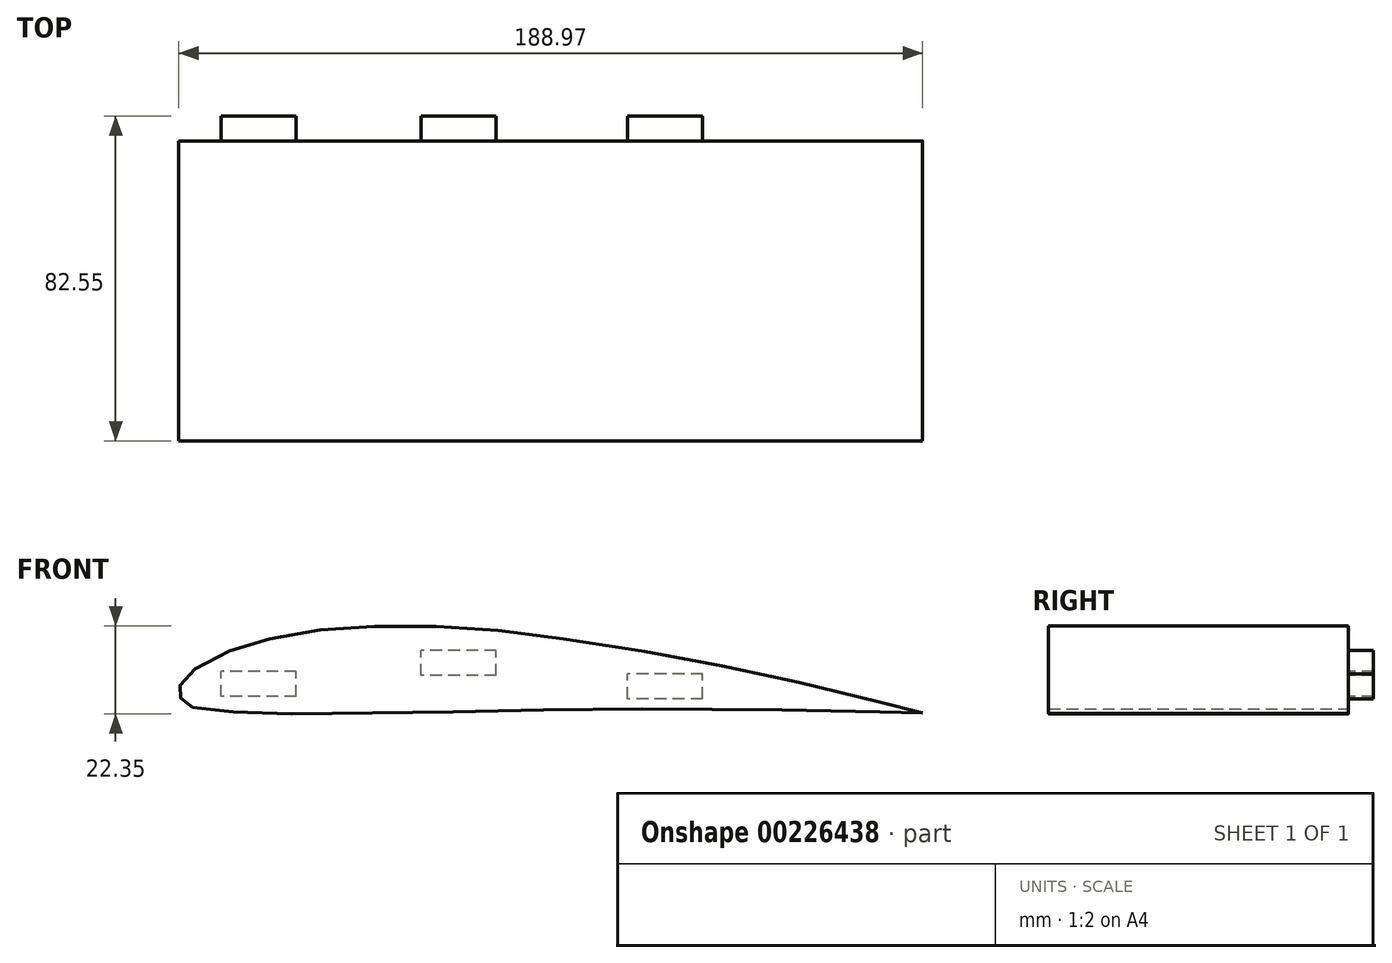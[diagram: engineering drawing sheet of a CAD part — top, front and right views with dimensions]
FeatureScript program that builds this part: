
annotation { "Feature Type Name" : "Feature", "Feature Type Description" : "" }
export const myFeature = defineFeature(function(context is Context, id is Id, definition is map)
    precondition{}
    {
        {
            var Q0;
            Q0=qCreatedBy(makeId("Front.planeOp"),FACE);
            var sketch = newSketch(context, id + "F0", { "sketchPlane" : qUnion([Q0])});
            skFitSpline(sketch, "E0.0", {"points": [v(113.13, -7.74) * mm, v(113.1, -7.8) * mm, v(110.34, -7.7) * mm, v(99.32, -7.43) * mm, v(55.98, -6.77) * mm, v(16.87, -7.02) * mm, v(15.68, -7.03) * mm, v(-47.47, -7.98) * mm, v(-59.24, -7.55) * mm, v(-66.72, -7.33) * mm, v(-71.5, -6.53) * mm, v(-72.72, -6.16) * mm, v(-73.48, -5.82) * mm, v(-74.18, -5.33) * mm, v(-74.78, -4.74) * mm, v(-75.21, -4.15) * mm, v(-75.5, -3.61) * mm, v(-75.69, -3.09) * mm, v(-75.76, -2.76) * mm, v(-75.8, -2.28) * mm, v(-75.77, -1.79) * mm, v(-75.64, -1.22) * mm, v(-75.39, -0.56) * mm, v(-74.8, 0.42) * mm, v(-73.97, 1.42) * mm, v(-72.44, 2.82) * mm, v(-70, 4.46) * mm, v(-65.33, 6.96) * mm, v(-60.69, 8.94) * mm, v(-55.6, 10.4) * mm, v(-48, 12.06) * mm, v(-39.71, 13.3) * mm, v(-30.48, 14.09) * mm, v(-19.95, 14.34) * mm, v(-7.36, 14.13) * mm, v(4.86, 13.21) * mm, v(17.45, 11.72) * mm, v(37.4, 8.66) * mm, v(57.72, 5.15) * mm, v(75.8, 1.3) * mm, v(97.79, -3.81) * mm, v(110.28, -7.09) * mm, v(113.15, -7.68) * mm, v(113.13, -7.74) * mm]});
            skPoint(sketch, "E1", {"position": v(-75.8, -2.17) * mm});
            skPoint(sketch, "E2", {"position": v(112.92, -7.77) * mm});
            skLineSegment(sketch, "E3.bottom", {"start": v(-45.95, -3.58) * mm, "end": v(-65, -3.58) * mm});
            skLineSegment(sketch, "E3.top", {"start": v(-45.95, 2.77) * mm, "end": v(-65, 2.77) * mm});
            skLineSegment(sketch, "E3.left", {"start": v(-45.95, -3.58) * mm, "end": v(-45.95, 2.77) * mm});
            skLineSegment(sketch, "E3.right", {"start": v(-65, -3.58) * mm, "end": v(-65, 2.77) * mm});
            skPoint(sketch, "E3.middle", {"position": v(-55.47, -0.4) * mm});
            skLineSegment(sketch, "E4.bottom", {"start": v(4.85, 1.75) * mm, "end": v(-14.2, 1.75) * mm});
            skLineSegment(sketch, "E4.top", {"start": v(4.85, 8.1) * mm, "end": v(-14.2, 8.1) * mm});
            skLineSegment(sketch, "E4.left", {"start": v(4.85, 1.75) * mm, "end": v(4.85, 8.1) * mm});
            skLineSegment(sketch, "E4.right", {"start": v(-14.2, 1.75) * mm, "end": v(-14.2, 8.1) * mm});
            skPoint(sketch, "E4.middle", {"position": v(-4.67, 4.93) * mm});
            skLineSegment(sketch, "E5.bottom", {"start": v(57.28, -4.16) * mm, "end": v(38.23, -4.16) * mm});
            skLineSegment(sketch, "E5.top", {"start": v(57.28, 2.2) * mm, "end": v(38.23, 2.2) * mm});
            skLineSegment(sketch, "E5.left", {"start": v(57.28, -4.16) * mm, "end": v(57.28, 2.2) * mm});
            skLineSegment(sketch, "E5.right", {"start": v(38.23, -4.16) * mm, "end": v(38.23, 2.2) * mm});
            skPoint(sketch, "E5.middle", {"position": v(47.76, -0.98) * mm});
            skLineSegment(sketch, "E6", {"start": v(112.92, -7.77) * mm, "end": v(-97.83, -7.77) * mm, "construction": true});
            skSolve(sketch);
        }
        {
            var Q0;
            Q0=makeQuery(id+"F0.imprint","IMPRINT",FACE,{"disambiguationData":[TD([[makeQuery(id+"F0.imprint","IMPRINT",EDGE,{"derivedFrom":sQuery(id+"F0.wireOp",EDGE,"E3.bottom")}),-1.0]])]});
            var Q1;
            Q1=makeQuery(id+"F0.imprint","IMPRINT",FACE,{"disambiguationData":[TD([[makeQuery(id+"F0.imprint","IMPRINT",EDGE,{"derivedFrom":sQuery(id+"F0.wireOp",EDGE,"E4.bottom")}),-1.0]])]});
            var Q2;
            Q2=makeQuery(id+"F0.imprint","IMPRINT",FACE,{"disambiguationData":[TD([[makeQuery(id+"F0.imprint","IMPRINT",EDGE,{"derivedFrom":sQuery(id+"F0.wireOp",EDGE,"E0.0")}),-1.0]])]});
            var Q3;
            Q3=makeQuery(id+"F0.imprint","IMPRINT",FACE,{"disambiguationData":[TD([[makeQuery(id+"F0.imprint","IMPRINT",EDGE,{"derivedFrom":sQuery(id+"F0.wireOp",EDGE,"E5.bottom")}),-1.0]])]});
            extrude(context, id + "F1", {"entities" : qUnion([Q0, Q1, Q2, Q3]), "depth" : 76.2 * mm});
        }
        {
            var Q0;
            Q0=makeQuery(id+"F0.imprint","IMPRINT",FACE,{"disambiguationData":[TD([[makeQuery(id+"F0.imprint","IMPRINT",EDGE,{"derivedFrom":sQuery(id+"F0.wireOp",EDGE,"E3.bottom")}),-1.0]])]});
            var Q1;
            Q1=makeQuery(id+"F0.imprint","IMPRINT",FACE,{"disambiguationData":[TD([[makeQuery(id+"F0.imprint","IMPRINT",EDGE,{"derivedFrom":sQuery(id+"F0.wireOp",EDGE,"E4.bottom")}),-1.0]])]});
            var Q2;
            Q2=makeQuery(id+"F0.imprint","IMPRINT",FACE,{"disambiguationData":[TD([[makeQuery(id+"F0.imprint","IMPRINT",EDGE,{"derivedFrom":sQuery(id+"F0.wireOp",EDGE,"E5.bottom")}),-1.0]])]});
            extrude(context, id + "F2", {"entities" : qUnion([Q0, Q1, Q2]), "operationType" : NewBodyOperationType.ADD, "oppositeDirection" : true, "depth" : 6.35 * mm});
        }
    });
